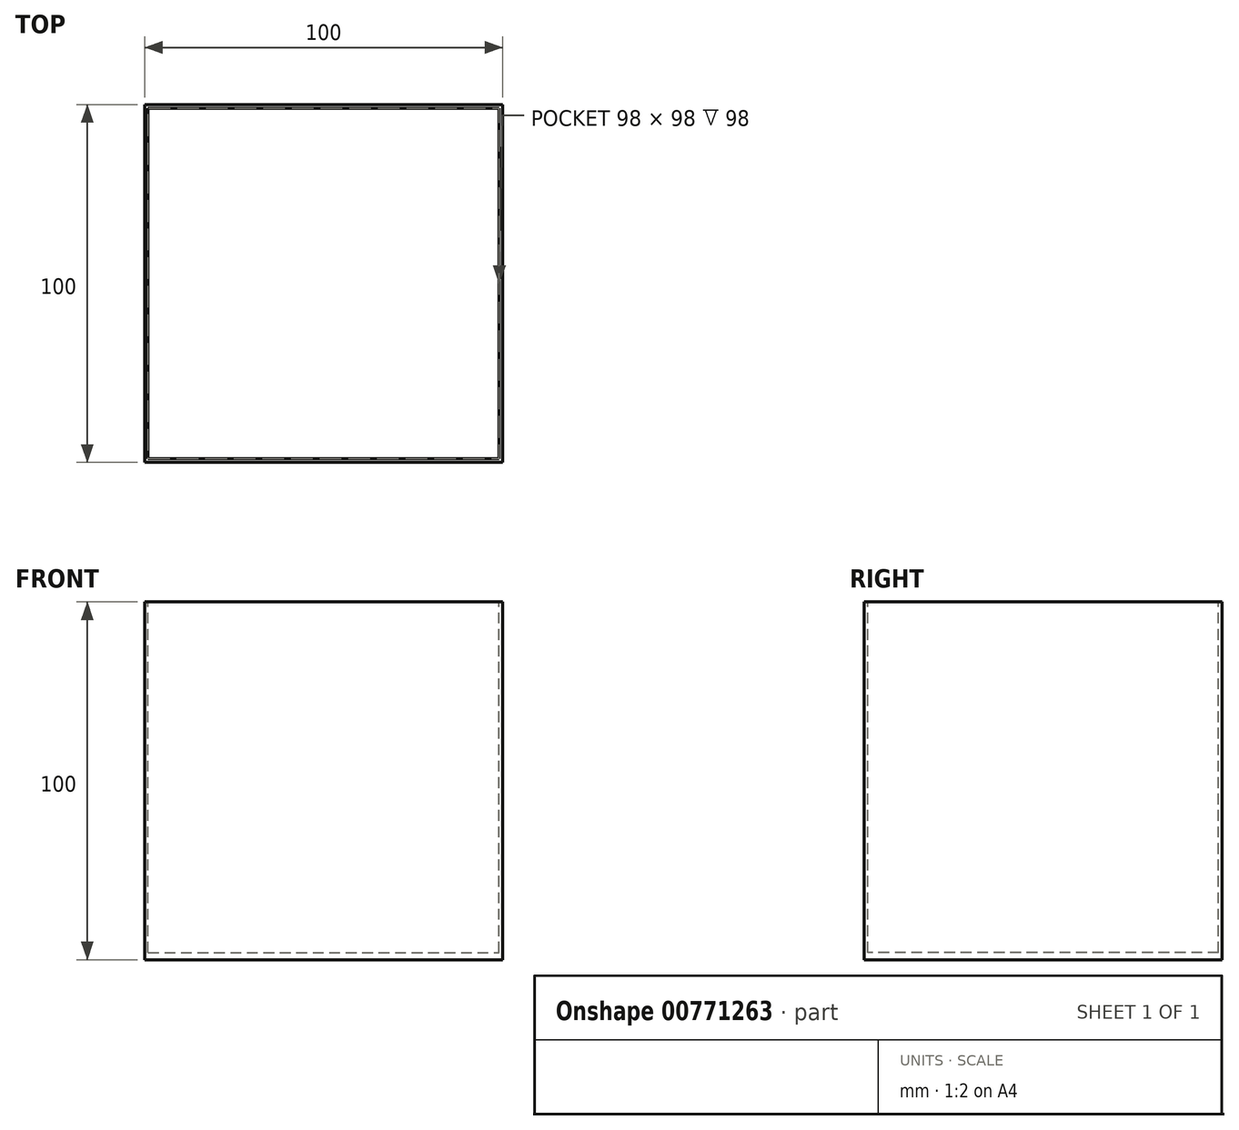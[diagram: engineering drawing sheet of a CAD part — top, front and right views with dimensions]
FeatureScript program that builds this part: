
annotation { "Feature Type Name" : "Feature", "Feature Type Description" : "" }
export const myFeature = defineFeature(function(context is Context, id is Id, definition is map)
    precondition{}
    {
        {
            var Q0;
            Q0=qCreatedBy(makeId("Front.planeOp"),FACE);
            var sketch = newSketch(context, id + "F0", { "sketchPlane" : qUnion([Q0])});
            skLineSegment(sketch, "E0.bottom", {"start": v(-50, 50) * mm, "end": v(50, 50) * mm});
            skLineSegment(sketch, "E0.top", {"start": v(-50, -50) * mm, "end": v(50, -50) * mm});
            skLineSegment(sketch, "E0.left", {"start": v(-50, 50) * mm, "end": v(-50, -50) * mm});
            skLineSegment(sketch, "E0.right", {"start": v(50, 50) * mm, "end": v(50, -50) * mm});
            skPoint(sketch, "E0.middle", {"position": v(0, 0) * mm});
            skSolve(sketch);
        }
        {
            var Q0;
            Q0=makeQuery(id+"F0.imprint","IMPRINT",FACE,{"disambiguationData":[TD([[makeQuery(id+"F0.imprint","IMPRINT",EDGE,{"derivedFrom":sQuery(id+"F0.wireOp",EDGE,"E0.bottom")}),-1.0]])]});
            extrude(context, id + "F1", {"entities" : qUnion([Q0]), "oppositeDirection" : true, "depth" : 100 * mm, "offsetDistance" : 25 * mm});
        }
        {
            var Q0;
            Q0=makeQuery(id+"F1.opExtrude","SWEPT_FACE",FACE,{"disambiguationData":[OSD([sQuery(id+"F0.wireOp",EDGE,"E0.bottom")])]});
            var sketch = newSketch(context, id + "F2", { "sketchPlane" : qUnion([Q0])});
            skLineSegment(sketch, "E1.bottom", {"start": v(-49, 99) * mm, "end": v(49, 99) * mm});
            skLineSegment(sketch, "E1.top", {"start": v(-49, 1) * mm, "end": v(49, 1) * mm});
            skLineSegment(sketch, "E1.left", {"start": v(-49, 99) * mm, "end": v(-49, 1) * mm});
            skLineSegment(sketch, "E1.right", {"start": v(49, 99) * mm, "end": v(49, 1) * mm});
            skSolve(sketch);
        }
        {
            var Q0;
            Q0=makeQuery(id+"F2.imprint","IMPRINT",FACE,{"disambiguationData":[TD([[makeQuery(id+"F2.imprint","IMPRINT",EDGE,{"derivedFrom":sQuery(id+"F2.wireOp",EDGE,"E1.bottom")}),-1.0]])]});
            extrude(context, id + "F3", {"entities" : qUnion([Q0]), "operationType" : NewBodyOperationType.REMOVE, "oppositeDirection" : true, "depth" : 98 * mm, "offsetDistance" : 25 * mm});
        }
    });
